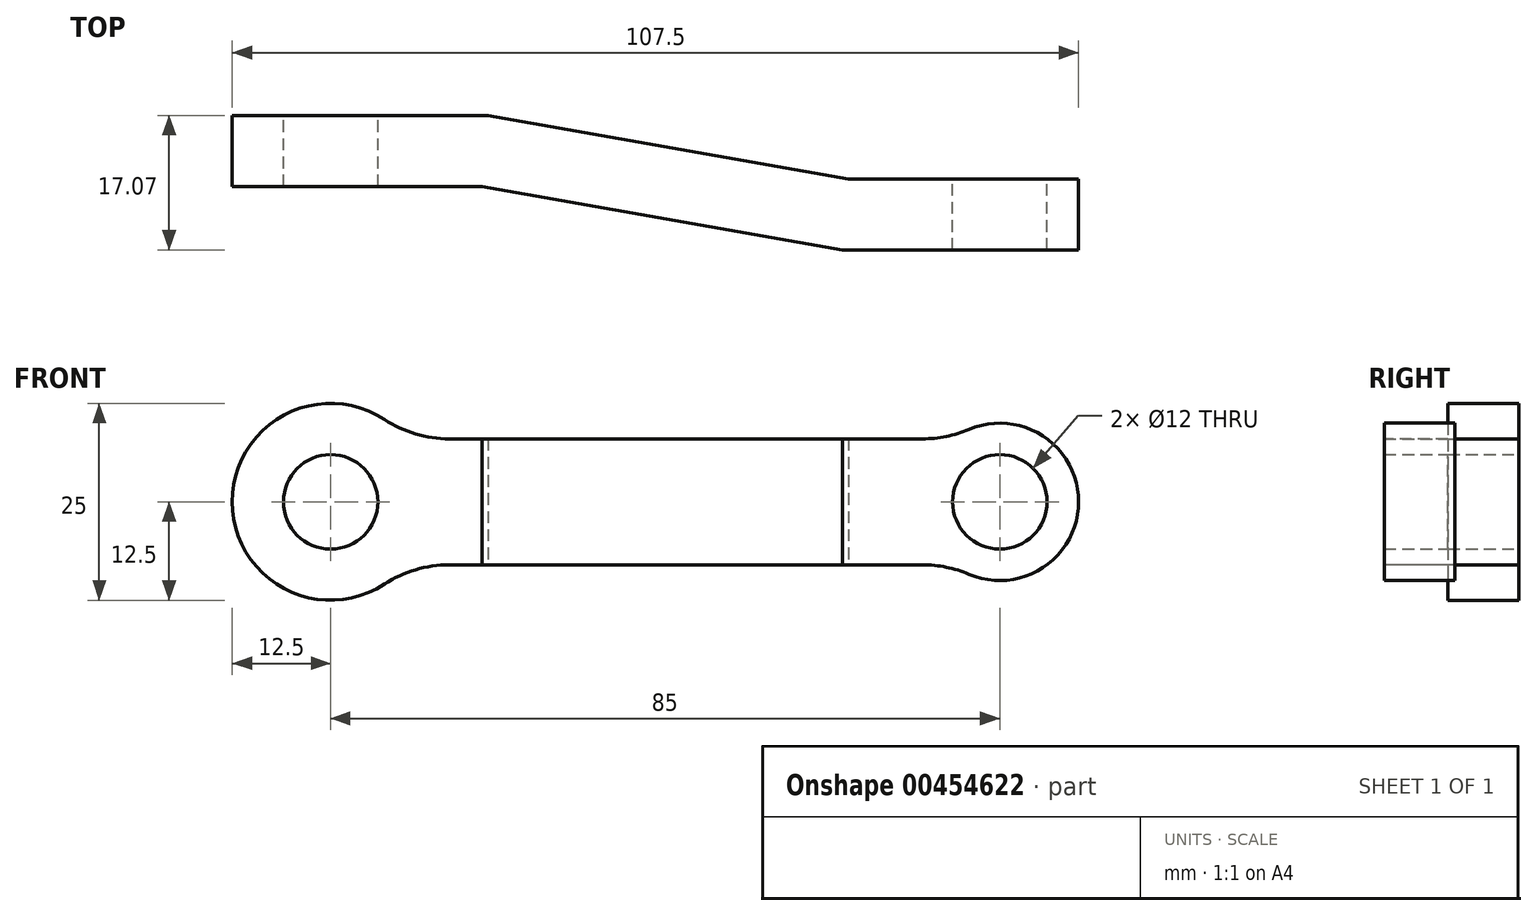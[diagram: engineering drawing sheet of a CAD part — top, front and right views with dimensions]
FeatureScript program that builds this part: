
annotation { "Feature Type Name" : "Feature", "Feature Type Description" : "" }
export const myFeature = defineFeature(function(context is Context, id is Id, definition is map)
    precondition{}
    {
        {
            var Q0;
            Q0=qCreatedBy(makeId("Front.planeOp"),FACE);
            var sketch = newSketch(context, id + "F0", { "sketchPlane" : qUnion([Q0])});
            skCircle(sketch, "E0", {"center": v(0, 0) * mm, "radius": 12.5 * mm});
            skCircle(sketch, "E1", {"center": v(85, 0) * mm, "radius": 10 * mm});
            skLineSegment(sketch, "E2", {"start": v(85, 0) * mm, "end": v(0, 0) * mm, "construction": true});
            skLineSegment(sketch, "E3", {"start": v(9.6, 8) * mm, "end": v(79, 8) * mm});
            skLineSegment(sketch, "E4.MirrorCS", {"start": v(9.6, -8) * mm, "end": v(79, -8) * mm});
            skCircle(sketch, "E5", {"center": v(0, 0) * mm, "radius": 6 * mm});
            skCircle(sketch, "E6", {"center": v(85, 0) * mm, "radius": 6 * mm});
            skSolve(sketch);
        }
        {
            var Q0;
            Q0 = qSketchRegion(id + "F0", true);
            extrude(context, id + "F1", {"entities" : qUnion([Q0]), "depth" : 25 * mm});
        }
        {
            var Q0;
            Q0=qCreatedBy(makeId("Top.planeOp"),FACE);
            var sketch = newSketch(context, id + "F2", { "sketchPlane" : qUnion([Q0])});
            skLineSegment(sketch, "E7", {"start": v(95, -8.07) * mm, "end": v(65.79, -8.07) * mm});
            skLineSegment(sketch, "E8", {"start": v(65.79, -8.07) * mm, "end": v(20, 0) * mm});
            skLineSegment(sketch, "E9", {"start": v(20, 0) * mm, "end": v(-12.5, 0) * mm});
            skLineSegment(sketch, "E10.0", {"start": v(19.21, -9) * mm, "end": v(-12.5, -9) * mm});
            skLineSegment(sketch, "E10.1", {"start": v(65, -17.07) * mm, "end": v(19.21, -9) * mm});
            skLineSegment(sketch, "E10.2", {"start": v(95, -17.07) * mm, "end": v(65, -17.07) * mm});
            skLineSegment(sketch, "E11", {"start": v(95, -8.07) * mm, "end": v(95, -17.07) * mm});
            skLineSegment(sketch, "E12", {"start": v(-12.5, 0) * mm, "end": v(-12.5, -9) * mm});
            skLineSegment(sketch, "E13", {"start": v(-12.5, -25) * mm, "end": v(-12.5, 0) * mm});
            skLineSegment(sketch, "E14", {"start": v(95, -0.07) * mm, "end": v(95, -25) * mm});
            skSolve(sketch);
        }
        {
            var Q0;
            Q0 = qSketchRegion(id + "F2", true);
            extrude(context, id + "F3", {"entities" : qUnion([Q0]), "operationType" : NewBodyOperationType.INTERSECT, "endBound" : BoundingType.SYMMETRIC, "depth" : 25 * mm});
        }
        {
            var Q0;
            Q0=makeQuery(id+"F1.opExtrude","SWEPT_EDGE",EDGE,{"disambiguationData":[OSD([sQuery(id+"F0.wireOp",EDGE,"E1"),sQuery(id+"F0.wireOp",EDGE,"E4.MirrorCS")])]});
            var Q1;
            Q1=makeQuery(id+"F1.opExtrude","SWEPT_EDGE",EDGE,{"disambiguationData":[OSD([sQuery(id+"F0.wireOp",EDGE,"E0"),sQuery(id+"F0.wireOp",EDGE,"E4.MirrorCS")])]});
            var Q2;
            Q2=makeQuery(id+"F1.opExtrude","SWEPT_EDGE",EDGE,{"disambiguationData":[OSD([sQuery(id+"F0.wireOp",EDGE,"E0"),sQuery(id+"F0.wireOp",EDGE,"E3")])]});
            var Q3;
            Q3=makeQuery(id+"F1.opExtrude","SWEPT_EDGE",EDGE,{"disambiguationData":[OSD([sQuery(id+"F0.wireOp",EDGE,"E1"),sQuery(id+"F0.wireOp",EDGE,"E3")])]});
            fillet(context, id + "F4", {"entities" : qUnion([Q0, Q1, Q2, Q3]), "radius" : 15 * mm, "tangentPropagation" : true, "allowEdgeOverflow" : false});
        }
    });
